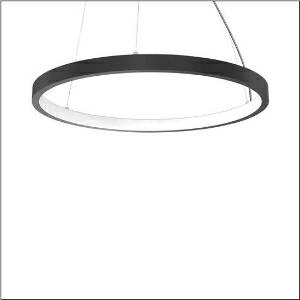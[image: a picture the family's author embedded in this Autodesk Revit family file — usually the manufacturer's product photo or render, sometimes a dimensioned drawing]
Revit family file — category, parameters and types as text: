
# Revit family: silica_r__21_ring-i_5pjbi4d3104a_5ad9
name_source: partatom
category: Lighting Fixtures
units: mm (PartAtom-declared; Revit-internal decimal feet)

## family parameters
Cut with Voids When Loaded = No
Host = Face
Light Source = No
Part Type = Normal
Room Calculation Point = No
Round Connector Dimension = Use Diameter
Shared = No

## types (1)
- Silica® 21 Ring-I (1 x LED, 8890 lm, 140 W, 4000K)
    Apparent Load = 140 VA
    CIE Flux Codes = 22 48 76 50 101
    Color Rendering = 80
    Color Temperature = 4000K
    Default Elevation = 1800 mm
    Description = Silica® 21 Ring-I, suspended luminaire, of PMMA, frosted, light emission: inner ring side luminous distribution, primary light characteristic: symmetric, installation type: suspended mounting, LED, rated luminous flux: 8.890lm, luminous efficacy: 64lm/W, light colour: 840, colour temperature: 4000K, control gear: DALI 2, with terminal, 5-pole, mains connection: 230V, AC/DC, 0/50..60Hz, rated input power: 140W, housing, of extruded aluminium section, jet black (RAL 9005), diameter: 1.470mm, ceiling canopy, jet black (RAL 9005), protection rating (lamp compartment): IP40, insulation class (complete): insulation class I (protective earthing), certification: CE, impact resistance: IK02, permissible operating ambient temperature: 0..+35°C, packaging unit: 1 piece
    Height = 48 mm  [stored 0.15748 ft]
    Lamp = 1 x LED
    Lamp Light Flux = 8890 lm
    Lamp Power = 140 W
    Lamp count = 1
    Length = 1470 mm
    Luminous efficacy = 64 lm/W
    Manufacturer = Siteco
    ModVariant = No
    Model = 5PJBI4D3104A
    Mounting Place = Ceiling
    Mounting Type = Pendant
    Number of Poles = 1
    OnlyDefault = Yes
    Power Factor = 1
    Product Name = Silica® 21 Ring-I
    Product group = suspended luminaire
    ProductGroupID = 905
    Protection Class = Protection class I
    Protection Degree = IP 40
    RLX_Detail_Level = 1
    RLX_Emergency_Light_Flux = 0 lm
    RLX_Emergency_Type = 0
    RLX_Emergency_Type_DB = No
    RlxData = <blob elided: 20409 chars, md5=b151d46c>
    Socket = socket
    Standby Power = 0 W
    System Light Flux = 8890 lm
    System Power = 140 W
    Type Comments = Product without accessories
    Type Image = l_1258373.jpg
    URL = http://relux.com
    VarID = ---
    Voltage = 0 V
    Weight = 0.00 kg
    Width = 0 mm  [stored 0 ft]

note: [stored X ft] marks values corroborated as IEEE doubles in the binary element streams (Revit-internal decimal feet)

## geometry (parser evidence)
native form markers: Blend x4, Sweep x14
no freeform markers — native parametric forms only
